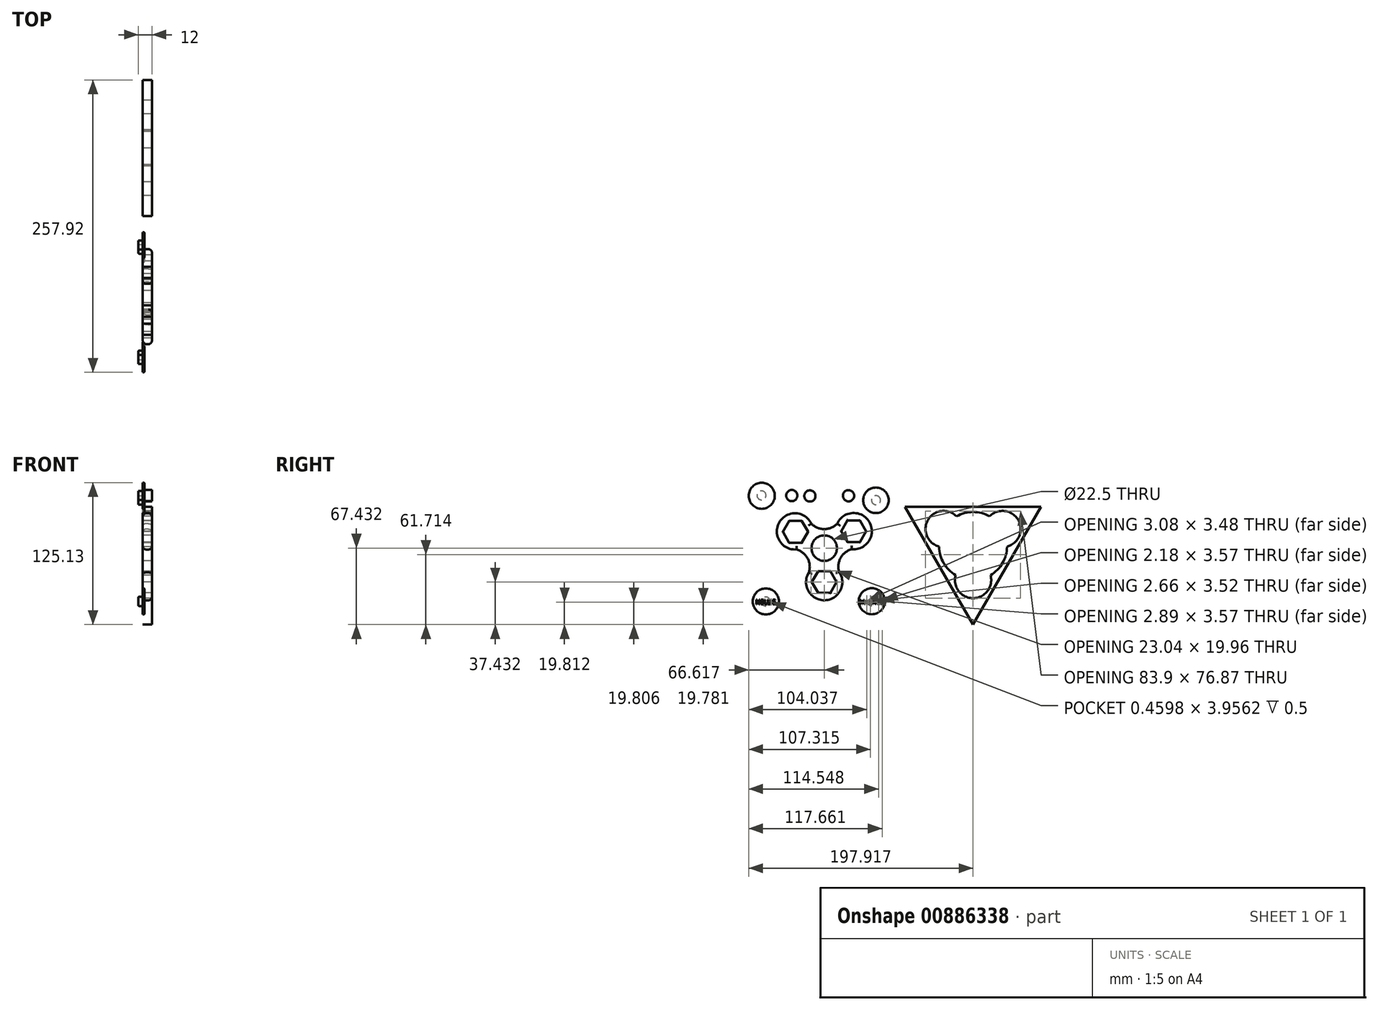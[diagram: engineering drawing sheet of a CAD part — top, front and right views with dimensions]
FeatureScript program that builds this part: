
annotation { "Feature Type Name" : "Feature", "Feature Type Description" : "" }
export const myFeature = defineFeature(function(context is Context, id is Id, definition is map)
    precondition{}
    {
        {
            var Q0;
            Q0=qCreatedBy(makeId("Right.planeOp"),FACE);
            var sketch = newSketch(context, id + "F0", { "sketchPlane" : qUnion([Q0])});
            skPoint(sketch, "E0.end.orphan", {"position": v(-35.82, -2.21) * mm});
            skPoint(sketch, "E1.0.midPoint", {"position": v(26.53, 28.89) * mm});
            skLineSegment(sketch, "E2.0", {"start": v(-31.38, 29.38) * mm, "end": v(-31.17, 29.38) * mm});
            skPoint(sketch, "E2.0.midPoint", {"position": v(-25.1, 29.46) * mm});
            skPoint(sketch, "E3.0.midPoint", {"position": v(-0.22, -15.81) * mm});
            skArc(sketch, "E4", {"start": v(24.19, 4.5) * mm, "mid": v(39.61, 28.42) * mm, "end": v(11.18, 27.02) * mm});
            skArc(sketch, "E5", {"start": v(-13.75, -16.02) * mm, "mid": v(0.24, -40.57) * mm, "end": v(12.78, -15.26) * mm});
            skPoint(sketch, "E6.startSnap0", {"position": v(-7.81, -20.2) * mm});
            skLineSegment(sketch, "E7", {"start": v(71.08, 41.9) * mm, "end": v(191.08, 41.9) * mm});
            skLineSegment(sketch, "E8", {"start": v(191.08, 41.9) * mm, "end": v(131.08, -62.01) * mm});
            skLineSegment(sketch, "E9", {"start": v(131.08, -62.01) * mm, "end": v(71.08, 41.9) * mm});
            skPoint(sketch, "E10.end.orphan", {"position": v(95.48, -0.36) * mm});
            skLineSegment(sketch, "E11", {"start": v(131.08, -62.01) * mm, "end": v(101.08, -10.05) * mm});
            skLineSegment(sketch, "E12", {"start": v(191.08, 41.9) * mm, "end": v(101.08, -10.05) * mm});
            skLineSegment(sketch, "E13", {"start": v(131.08, -62.01) * mm, "end": v(161.08, -10.05) * mm});
            skLineSegment(sketch, "E14", {"start": v(161.08, -10.05) * mm, "end": v(71.08, 41.9) * mm});
            skLineSegment(sketch, "E15", {"start": v(71.08, 41.9) * mm, "end": v(98.79, 25.9) * mm});
            skLineSegment(sketch, "E16", {"start": v(191.08, 41.9) * mm, "end": v(163.36, 25.9) * mm});
            skLineSegment(sketch, "E17", {"start": v(131.08, -62.01) * mm, "end": v(131.08, -30.01) * mm});
            skCircle(sketch, "E18", {"center": v(131.08, 7.27) * mm, "radius": 11 * mm});
            skCircle(sketch, "E19", {"center": v(131.08, 7.27) * mm, "radius": 16 * mm});
            skCircle(sketch, "E20", {"center": v(131.08, 7.27) * mm, "radius": 30 * mm});
            skCircle(sketch, "E21", {"center": v(157.06, 22.27) * mm, "radius": 11 * mm});
            skCircle(sketch, "E22", {"center": v(105.1, 22.27) * mm, "radius": 11 * mm});
            skLineSegment(sketch, "E23", {"start": v(131.08, -30.01) * mm, "end": v(131.08, 40.66) * mm});
            skCircle(sketch, "E24", {"center": v(131.08, -22.73) * mm, "radius": 11 * mm});
            skCircle(sketch, "E25.cCircle", {"center": v(157.06, 22.27) * mm, "radius": 8.96 * mm, "construction": true});
            skLineSegment(sketch, "E25.0", {"start": v(151.89, 31.23) * mm, "end": v(162.23, 31.23) * mm});
            skLineSegment(sketch, "E25.1", {"start": v(162.23, 31.23) * mm, "end": v(167.4, 22.27) * mm});
            skLineSegment(sketch, "E25.2", {"start": v(167.4, 22.27) * mm, "end": v(162.23, 13.31) * mm});
            skLineSegment(sketch, "E25.3", {"start": v(162.23, 13.31) * mm, "end": v(151.89, 13.31) * mm});
            skLineSegment(sketch, "E25.4", {"start": v(151.89, 13.31) * mm, "end": v(146.71, 22.27) * mm});
            skLineSegment(sketch, "E25.5", {"start": v(146.71, 22.27) * mm, "end": v(151.89, 31.23) * mm});
            skPoint(sketch, "E25.0.midPoint", {"position": v(157.06, 31.23) * mm});
            skCircle(sketch, "E26.cCircle", {"center": v(105.1, 22.27) * mm, "radius": 8.96 * mm, "construction": true});
            skLineSegment(sketch, "E26.0", {"start": v(99.92, 31.23) * mm, "end": v(110.27, 31.23) * mm});
            skLineSegment(sketch, "E26.1", {"start": v(110.27, 31.23) * mm, "end": v(115.44, 22.27) * mm});
            skLineSegment(sketch, "E26.2", {"start": v(115.44, 22.27) * mm, "end": v(110.27, 13.31) * mm});
            skLineSegment(sketch, "E26.3", {"start": v(110.27, 13.31) * mm, "end": v(99.92, 13.31) * mm});
            skLineSegment(sketch, "E26.4", {"start": v(99.92, 13.31) * mm, "end": v(94.75, 22.27) * mm});
            skLineSegment(sketch, "E26.5", {"start": v(94.75, 22.27) * mm, "end": v(99.92, 31.23) * mm});
            skPoint(sketch, "E26.0.midPoint", {"position": v(105.1, 31.23) * mm});
            skCircle(sketch, "E27.cCircle", {"center": v(131.08, -22.73) * mm, "radius": 8.77 * mm, "construction": true});
            skLineSegment(sketch, "E27.0", {"start": v(126.02, -13.97) * mm, "end": v(136.14, -13.97) * mm});
            skLineSegment(sketch, "E27.1", {"start": v(136.14, -13.97) * mm, "end": v(141.2, -22.73) * mm});
            skLineSegment(sketch, "E27.2", {"start": v(141.2, -22.73) * mm, "end": v(136.14, -31.5) * mm});
            skLineSegment(sketch, "E27.3", {"start": v(136.14, -31.5) * mm, "end": v(126.02, -31.5) * mm});
            skLineSegment(sketch, "E27.4", {"start": v(126.02, -31.5) * mm, "end": v(120.95, -22.73) * mm});
            skLineSegment(sketch, "E27.5", {"start": v(120.95, -22.73) * mm, "end": v(126.02, -13.97) * mm});
            skPoint(sketch, "E27.0.midPoint", {"position": v(131.08, -13.97) * mm});
            skCircle(sketch, "E28", {"center": v(157.06, 22.27) * mm, "radius": 16 * mm});
            skCircle(sketch, "E29", {"center": v(131.08, -22.73) * mm, "radius": 16 * mm});
            skCircle(sketch, "E30", {"center": v(105.1, 22.27) * mm, "radius": 16 * mm});
            skCircle(sketch, "E31", {"center": v(131.08, 7.27) * mm, "radius": 20 * mm});
            skArc(sketch, "E32", {"start": v(116.5, 33.49) * mm, "mid": v(131.08, 27.63) * mm, "end": v(145.65, 33.49) * mm});
            skArc(sketch, "E33", {"start": v(161.07, 6.78) * mm, "mid": v(148.55, -2.82) * mm, "end": v(146.5, -18.46) * mm});
            skArc(sketch, "E34", {"start": v(115.46, -18.35) * mm, "mid": v(113.52, -2.78) * mm, "end": v(101.08, 6.78) * mm});
            skPoint(sketch, "E34.startSnap0", {"position": v(123.49, -18.35) * mm});
            skArc(sketch, "E35", {"start": v(24.19, 4.5) * mm, "mid": v(14.34, -2.99) * mm, "end": v(12.78, -15.26) * mm});
            skArc(sketch, "E36", {"start": v(-11.63, 27.02) * mm, "mid": v(-0.22, 22.24) * mm, "end": v(11.18, 27.02) * mm});
            skArc(sketch, "E37.trimOffspring", {"start": v(-15.84, -20.2) * mm, "mid": v(-15.74, -20.25) * mm, "end": v(-15.64, -20.31) * mm});
            skArc(sketch, "E38.trimOffspring", {"start": v(-11.63, 27.02) * mm, "mid": v(-39.88, 28.17) * mm, "end": v(-24.78, 4.26) * mm});
            skArc(sketch, "E39.trimOffspring", {"start": v(-13.75, -16.02) * mm, "mid": v(-14.94, -3.53) * mm, "end": v(-24.78, 4.26) * mm});
            skPoint(sketch, "E2.cCircle.center.orphan", {"position": v(-25.1, 20.5) * mm});
            skPoint(sketch, "E40.orphan", {"position": v(59.78, 40.06) * mm});
            skPoint(sketch, "E41.start.orphan", {"position": v(29.78, -11.9) * mm});
            skPoint(sketch, "E42.end.orphan", {"position": v(-30.22, -11.9) * mm});
            skPoint(sketch, "E43.orphan", {"position": v(-0.22, -63.86) * mm});
            skPoint(sketch, "E44.orphan", {"position": v(-60.22, 40.06) * mm});
            skCircle(sketch, "E45", {"center": v(-0.22, 5.42) * mm, "radius": 11.25 * mm});
            skLineSegment(sketch, "E46", {"start": v(-5.33, -15.9) * mm, "end": v(-5.8, -15.1) * mm});
            skLineSegment(sketch, "E47.0", {"start": v(-5.7, -15.1) * mm, "end": v(5.25, -15.1) * mm});
            skLineSegment(sketch, "E47.1", {"start": v(5.25, -15.1) * mm, "end": v(10.72, -24.58) * mm});
            skLineSegment(sketch, "E47.2", {"start": v(10.72, -24.58) * mm, "end": v(5.25, -34.06) * mm});
            skLineSegment(sketch, "E47.3", {"start": v(5.25, -34.06) * mm, "end": v(-5.7, -34.06) * mm});
            skLineSegment(sketch, "E47.4", {"start": v(-5.7, -34.06) * mm, "end": v(-11.17, -24.58) * mm});
            skLineSegment(sketch, "E47.5", {"start": v(-11.17, -24.58) * mm, "end": v(-5.7, -15.1) * mm});
            skPoint(sketch, "E47.0.midPoint", {"position": v(-0.22, -15.1) * mm});
            skPoint(sketch, "E48.endSnap0", {"position": v(-33.8, 24.63) * mm});
            skPoint(sketch, "E2.1.start.orphan", {"position": v(-18.83, 29.53) * mm});
            skPoint(sketch, "E49.orphan", {"position": v(-36.22, 19.88) * mm});
            skPoint(sketch, "E48.end.orphan", {"position": v(-33.8, 34.15) * mm});
            skPoint(sketch, "E50.orphan", {"position": v(21.03, 28.32) * mm});
            skPoint(sketch, "E1.1.start.orphan", {"position": v(32.03, 29.46) * mm});
            skLineSegment(sketch, "E51.0", {"start": v(-31.12, 29.46) * mm, "end": v(-20, 29.46) * mm});
            skLineSegment(sketch, "E51.1", {"start": v(-20, 29.46) * mm, "end": v(-14.45, 19.84) * mm});
            skLineSegment(sketch, "E51.2", {"start": v(-14.45, 19.84) * mm, "end": v(-20, 10.21) * mm});
            skLineSegment(sketch, "E51.3", {"start": v(-20, 10.21) * mm, "end": v(-31.12, 10.21) * mm});
            skLineSegment(sketch, "E51.4", {"start": v(-31.12, 10.21) * mm, "end": v(-36.67, 19.84) * mm});
            skLineSegment(sketch, "E51.5", {"start": v(-36.67, 19.84) * mm, "end": v(-31.12, 29.46) * mm});
            skPoint(sketch, "E51.0.midPoint", {"position": v(-25.56, 29.46) * mm});
            skPoint(sketch, "E52.0.midPoint", {"position": v(25.76, 30.74) * mm});
            skLineSegment(sketch, "E53", {"start": v(-31.2, 29.32) * mm, "end": v(-31.45, 29.77) * mm});
            skLineSegment(sketch, "E54", {"start": v(36.75, 20.42) * mm, "end": v(36.76, 20.42) * mm});
            skLineSegment(sketch, "E55.0", {"start": v(20.26, 29.94) * mm, "end": v(31.25, 29.94) * mm});
            skLineSegment(sketch, "E55.1", {"start": v(31.25, 29.94) * mm, "end": v(36.75, 20.42) * mm});
            skLineSegment(sketch, "E55.2", {"start": v(36.75, 20.42) * mm, "end": v(31.25, 10.9) * mm});
            skLineSegment(sketch, "E55.3", {"start": v(31.25, 10.9) * mm, "end": v(20.26, 10.9) * mm});
            skLineSegment(sketch, "E55.4", {"start": v(20.26, 10.9) * mm, "end": v(14.77, 20.42) * mm});
            skLineSegment(sketch, "E55.5", {"start": v(14.77, 20.42) * mm, "end": v(20.26, 29.94) * mm});
            skPoint(sketch, "E55.0.midPoint", {"position": v(25.76, 29.94) * mm});
            skPoint(sketch, "E56.orphan", {"position": v(19.8, 10.1) * mm});
            skPoint(sketch, "E57.orphan", {"position": v(13.85, 20.42) * mm});
            skPoint(sketch, "E58.orphan", {"position": v(37.67, 20.42) * mm});
            skPoint(sketch, "E59.orphan", {"position": v(31.71, 30.74) * mm});
            skPoint(sketch, "E52.0.start.orphan", {"position": v(19.8, 30.74) * mm});
            skPoint(sketch, "E51.cCircle.center.orphan", {"position": v(-25.56, 19.84) * mm});
            skPoint(sketch, "E60.orphan", {"position": v(4.84, -15.81) * mm});
            skLineSegment(sketch, "E61.trimOffspring", {"start": v(-5.33, -15.9) * mm, "end": v(-5.28, -15.81) * mm});
            skPoint(sketch, "E62.orphan", {"position": v(-10.35, -24.58) * mm});
            skLineSegment(sketch, "E63.trimOffspring", {"start": v(-0.22, -15.81) * mm, "end": v(-0.22, -15.1) * mm});
            skLineSegment(sketch, "E64.trimOffspring", {"start": v(-0.22, 22.24) * mm, "end": v(-0.22, 38.8) * mm});
            skSolve(sketch);
        }
        {
            var Q0;
            Q0 = qSketchRegion(id + "F0", true);
            extrude(context, id + "F1", {"entities" : qUnion([Q0]), "depth" : 8 * mm, "offsetDistance" : 25 * mm});
        }
        {
            var Q0;
            Q0=qCreatedBy(makeId("Right.planeOp"),FACE);
            var sketch = newSketch(context, id + "F2", { "sketchPlane" : qUnion([Q0])});
            skCircle(sketch, "E65", {"center": v(-51.74, -41.64) * mm, "radius": 11.5 * mm});
            skCircle(sketch, "E66", {"center": v(-55.34, 51.62) * mm, "radius": 11.5 * mm});
            skSolve(sketch);
        }
        {
            var Q0;
            Q0 = qSketchRegion(id + "F2", true);
            extrude(context, id + "F3", {"entities" : qUnion([Q0]), "depth" : 1.5 * mm, "offsetDistance" : 25 * mm});
        }
        {
            var Q0;
            Q0=makeQuery(id+"F3.opExtrude","CAP_FACE",FACE,{"disambiguationData":[OSD([sQuery(id+"F2.wireOp",EDGE,"E65")])],"isStart":false});
            var sketch = newSketch(context, id + "F4", { "sketchPlane" : qUnion([Q0])});
            skText(sketch, "E67", { "text": "NELLIE\n", "fontName": "OpenSans-Regular.ttf"});
            const initialGuessF4  = {"E67": [-0.06069, -0.04405, 1, 0, 0.00399]};
            skSetInitialGuess(sketch, initialGuessF4);
            skSolve(sketch);
        }
        {
            var Q0;
            Q0 = qSketchRegion(id + "F4", true);
            extrude(context, id + "F5", {"entities" : qUnion([Q0]), "operationType" : NewBodyOperationType.REMOVE, "oppositeDirection" : true, "depth" : 0.5 * mm, "offsetDistance" : 25 * mm});
        }
        {
            var Q0;
            Q0=qCreatedBy(makeId("Right.planeOp"),FACE);
            var sketch = newSketch(context, id + "F6", { "sketchPlane" : qUnion([Q0])});
            skCircle(sketch, "E68", {"center": v(41.73, -41.46) * mm, "radius": 11.5 * mm});
            skCircle(sketch, "E69", {"center": v(45.36, 47.63) * mm, "radius": 11.26 * mm});
            skSolve(sketch);
        }
        {
            var Q0;
            Q0 = qSketchRegion(id + "F6", true);
            extrude(context, id + "F7", {"entities" : qUnion([Q0]), "depth" : 1.5 * mm, "offsetDistance" : 25 * mm});
        }
        {
            var Q0;
            Q0=makeQuery(id+"F7.opExtrude","CAP_FACE",FACE,{"disambiguationData":[OSD([sQuery(id+"F6.wireOp",EDGE,"E68")])],"isStart":false});
            var sketch = newSketch(context, id + "F8", { "sketchPlane" : qUnion([Q0])});
            skText(sketch, "E70", { "text": "MAGNUS", "fontName": "OpenSans-Regular.ttf"});
            const initialGuessF8  = {"E70": [0.03127, -0.04394, 1, 0, 0.0035]};
            skSetInitialGuess(sketch, initialGuessF8);
            skSolve(sketch);
        }
        {
            var Q0;
            Q0 = qSketchRegion(id + "F8", true);
            extrude(context, id + "F9", {"entities" : qUnion([Q0]), "operationType" : NewBodyOperationType.REMOVE, "oppositeDirection" : true, "depth" : 0.5 * mm, "offsetDistance" : 25 * mm});
        }
        {
            var Q0;
            Q0=makeQuery(id+"F7.opExtrude","CAP_FACE",FACE,{"disambiguationData":[OSD([sQuery(id+"F6.wireOp",EDGE,"E68")])],"isStart":true});
            var sketch = newSketch(context, id + "F10", { "sketchPlane" : qUnion([Q0])});
            skCircle(sketch, "E71", {"center": v(-41.73, -41.46) * mm, "radius": 4 * mm});
            skSolve(sketch);
        }
        {
            var Q0;
            Q0 = qSketchRegion(id + "F10", true);
            extrude(context, id + "F11", {"entities" : qUnion([Q0]), "operationType" : NewBodyOperationType.ADD, "depth" : 4 * mm, "offsetDistance" : 25 * mm});
        }
        {
            var Q0;
            Q0=makeQuery(id+"F3.opExtrude","CAP_FACE",FACE,{"disambiguationData":[OSD([sQuery(id+"F2.wireOp",EDGE,"E65")])],"isStart":true});
            var sketch = newSketch(context, id + "F12", { "sketchPlane" : qUnion([Q0])});
            skCircle(sketch, "E72", {"center": v(51.74, -41.64) * mm, "radius": 4 * mm});
            skCircle(sketch, "E73", {"center": v(-45.46, 47.7) * mm, "radius": 4 * mm});
            skCircle(sketch, "E74", {"center": v(55.55, 51.99) * mm, "radius": 4 * mm});
            skSolve(sketch);
        }
        {
            var Q0;
            Q0 = qSketchRegion(id + "F12", true);
            extrude(context, id + "F13", {"entities" : qUnion([Q0]), "operationType" : NewBodyOperationType.ADD, "depth" : 4 * mm, "offsetDistance" : 25 * mm});
        }
        {
            var Q0;
            Q0=makeQuery(id+"F1.opExtrude","CAP_EDGE",EDGE,{"disambiguationData":[OSD([sQuery(id+"F0.wireOp",EDGE,"E4")])],"isStart":false});
            var Q1;
            Q1=makeQuery(id+"F1.opExtrude","CAP_EDGE",EDGE,{"disambiguationData":[OSD([sQuery(id+"F0.wireOp",EDGE,"E36")])],"isStart":false});
            var Q2;
            Q2=makeQuery(id+"F1.opExtrude","CAP_EDGE",EDGE,{"disambiguationData":[OSD([sQuery(id+"F0.wireOp",EDGE,"E39.trimOffspring")])],"isStart":false});
            var Q3;
            Q3=makeQuery(id+"F1.opExtrude","CAP_EDGE",EDGE,{"disambiguationData":[OSD([sQuery(id+"F0.wireOp",EDGE,"E35")])],"isStart":false});
            var Q4;
            Q4=makeQuery(id+"F1.opExtrude","CAP_EDGE",EDGE,{"disambiguationData":[OSD([sQuery(id+"F0.wireOp",EDGE,"E5")])],"isStart":false});
            var Q5;
            Q5=makeQuery(id+"F1.opExtrude","CAP_EDGE",EDGE,{"disambiguationData":[OSD([sQuery(id+"F0.wireOp",EDGE,"E38.trimOffspring")])],"isStart":false});
            var Q6;
            Q6=makeQuery(id+"F1.opExtrude","CAP_EDGE",EDGE,{"disambiguationData":[OSD([sQuery(id+"F0.wireOp",EDGE,"E36")])],"isStart":true});
            var Q7;
            Q7=makeQuery(id+"F1.opExtrude","CAP_EDGE",EDGE,{"disambiguationData":[OSD([sQuery(id+"F0.wireOp",EDGE,"E4")])],"isStart":true});
            var Q8;
            Q8=makeQuery(id+"F1.opExtrude","CAP_EDGE",EDGE,{"disambiguationData":[OSD([sQuery(id+"F0.wireOp",EDGE,"E35")])],"isStart":true});
            var Q9;
            Q9=makeQuery(id+"F1.opExtrude","CAP_EDGE",EDGE,{"disambiguationData":[OSD([sQuery(id+"F0.wireOp",EDGE,"E39.trimOffspring")])],"isStart":true});
            var Q10;
            Q10=makeQuery(id+"F1.opExtrude","CAP_EDGE",EDGE,{"disambiguationData":[OSD([sQuery(id+"F0.wireOp",EDGE,"E38.trimOffspring")])],"isStart":true});
            var Q11;
            Q11=makeQuery(id+"F1.opExtrude","CAP_EDGE",EDGE,{"disambiguationData":[OSD([sQuery(id+"F0.wireOp",EDGE,"E5")])],"isStart":true});
            fillet(context, id + "F14", {"entities" : qUnion([Q0, Q1, Q2, Q3, Q4, Q5, Q6, Q7, Q8, Q9, Q10, Q11]), "radius" : 3 * mm, "tangentPropagation" : true, "allowEdgeOverflow" : false});
        }
        {
            var Q0;
            Q0=makeQuery(id+"F3.opExtrude","CAP_EDGE",EDGE,{"disambiguationData":[OSD([sQuery(id+"F2.wireOp",EDGE,"E65")])],"isStart":false});
            var Q1;
            Q1=makeQuery(id+"F7.opExtrude","CAP_EDGE",EDGE,{"disambiguationData":[OSD([sQuery(id+"F6.wireOp",EDGE,"E68")])],"isStart":false});
            var Q2;
            Q2=makeQuery(id+"F13.opExtrude","CAP_EDGE",EDGE,{"disambiguationData":[OSD([sQuery(id+"F12.wireOp",EDGE,"E72")])],"isStart":false});
            var Q3;
            Q3=makeQuery(id+"F11.opExtrude","CAP_EDGE",EDGE,{"disambiguationData":[OSD([sQuery(id+"F10.wireOp",EDGE,"E71")])],"isStart":false});
            var Q4;
            Q4=makeQuery(id+"F3.opExtrude","CAP_EDGE",EDGE,{"disambiguationData":[OSD([sQuery(id+"F2.wireOp",EDGE,"E66")])],"isStart":false});
            var Q5;
            Q5=makeQuery(id+"F7.opExtrude","CAP_EDGE",EDGE,{"disambiguationData":[OSD([sQuery(id+"F6.wireOp",EDGE,"E69")])],"isStart":false});
            fillet(context, id + "F15", {"entities" : qUnion([Q0, Q1, Q2, Q3, Q4, Q5]), "radius" : 0.8 * mm, "tangentPropagation" : true, "allowEdgeOverflow" : false});
        }
        {
            var Q0;
            Q0=makeQuery(id+"F1.opExtrude","CAP_EDGE",EDGE,{"disambiguationData":[OSD([sQuery(id+"F0.wireOp",EDGE,"E51.4")])],"isStart":false});
            var Q1;
            Q1=makeQuery(id+"F1.opExtrude","CAP_EDGE",EDGE,{"disambiguationData":[OSD([sQuery(id+"F0.wireOp",EDGE,"E51.0")])],"isStart":false});
            var Q2;
            Q2=makeQuery(id+"F1.opExtrude","CAP_EDGE",EDGE,{"disambiguationData":[OSD([sQuery(id+"F0.wireOp",EDGE,"E51.1")])],"isStart":false});
            var Q3;
            Q3=makeQuery(id+"F1.opExtrude","CAP_EDGE",EDGE,{"disambiguationData":[OSD([sQuery(id+"F0.wireOp",EDGE,"E51.2")])],"isStart":false});
            var Q4;
            Q4=makeQuery(id+"F1.opExtrude","CAP_EDGE",EDGE,{"disambiguationData":[OSD([sQuery(id+"F0.wireOp",EDGE,"E55.5")])],"isStart":false});
            var Q5;
            Q5=makeQuery(id+"F1.opExtrude","CAP_EDGE",EDGE,{"disambiguationData":[OSD([sQuery(id+"F0.wireOp",EDGE,"E55.3")])],"isStart":false});
            var Q6;
            Q6=makeQuery(id+"F1.opExtrude","CAP_EDGE",EDGE,{"disambiguationData":[OSD([sQuery(id+"F0.wireOp",EDGE,"E55.2")])],"isStart":false});
            var Q7;
            Q7=makeQuery(id+"F1.opExtrude","CAP_EDGE",EDGE,{"disambiguationData":[OSD([sQuery(id+"F0.wireOp",EDGE,"E55.1")])],"isStart":false});
            var Q8;
            Q8=makeQuery(id+"F1.opExtrude","CAP_EDGE",EDGE,{"disambiguationData":[OSD([sQuery(id+"F0.wireOp",EDGE,"E55.0")])],"isStart":false});
            var Q9;
            Q9=makeQuery(id+"F1.opExtrude","CAP_EDGE",EDGE,{"disambiguationData":[OSD([sQuery(id+"F0.wireOp",EDGE,"E47.0")])],"isStart":false});
            var Q10;
            Q10=makeQuery(id+"F1.opExtrude","CAP_EDGE",EDGE,{"disambiguationData":[OSD([sQuery(id+"F0.wireOp",EDGE,"E47.5")])],"isStart":false});
            var Q11;
            Q11=makeQuery(id+"F1.opExtrude","CAP_EDGE",EDGE,{"disambiguationData":[OSD([sQuery(id+"F0.wireOp",EDGE,"E47.4")])],"isStart":false});
            var Q12;
            Q12=makeQuery(id+"F1.opExtrude","CAP_EDGE",EDGE,{"disambiguationData":[OSD([sQuery(id+"F0.wireOp",EDGE,"E47.3")])],"isStart":false});
            var Q13;
            Q13=makeQuery(id+"F1.opExtrude","CAP_EDGE",EDGE,{"disambiguationData":[OSD([sQuery(id+"F0.wireOp",EDGE,"E47.2")])],"isStart":false});
            var Q14;
            Q14=makeQuery(id+"F1.opExtrude","CAP_EDGE",EDGE,{"disambiguationData":[OSD([sQuery(id+"F0.wireOp",EDGE,"E47.1")])],"isStart":false});
            var Q15;
            Q15=makeQuery(id+"F1.opExtrude","CAP_EDGE",EDGE,{"disambiguationData":[OSD([sQuery(id+"F0.wireOp",EDGE,"E55.2")])],"isStart":true});
            var Q16;
            Q16=makeQuery(id+"F1.opExtrude","CAP_EDGE",EDGE,{"disambiguationData":[OSD([sQuery(id+"F0.wireOp",EDGE,"E55.0")])],"isStart":true});
            var Q17;
            Q17=makeQuery(id+"F1.opExtrude","CAP_EDGE",EDGE,{"disambiguationData":[OSD([sQuery(id+"F0.wireOp",EDGE,"E55.5")])],"isStart":true});
            var Q18;
            Q18=makeQuery(id+"F1.opExtrude","CAP_EDGE",EDGE,{"disambiguationData":[OSD([sQuery(id+"F0.wireOp",EDGE,"E55.3")])],"isStart":true});
            var Q19;
            Q19=makeQuery(id+"F1.opExtrude","CAP_EDGE",EDGE,{"disambiguationData":[OSD([sQuery(id+"F0.wireOp",EDGE,"E51.2")])],"isStart":true});
            var Q20;
            Q20=makeQuery(id+"F1.opExtrude","CAP_EDGE",EDGE,{"disambiguationData":[OSD([sQuery(id+"F0.wireOp",EDGE,"E51.0")])],"isStart":true});
            var Q21;
            Q21=makeQuery(id+"F1.opExtrude","CAP_EDGE",EDGE,{"disambiguationData":[OSD([sQuery(id+"F0.wireOp",EDGE,"E51.4")])],"isStart":true});
            var Q22;
            Q22=makeQuery(id+"F1.opExtrude","CAP_EDGE",EDGE,{"disambiguationData":[OSD([sQuery(id+"F0.wireOp",EDGE,"E51.3")])],"isStart":true});
            var Q23;
            Q23=makeQuery(id+"F1.opExtrude","CAP_EDGE",EDGE,{"disambiguationData":[OSD([sQuery(id+"F0.wireOp",EDGE,"E47.0")])],"isStart":true});
            var Q24;
            Q24=makeQuery(id+"F1.opExtrude","CAP_EDGE",EDGE,{"disambiguationData":[OSD([sQuery(id+"F0.wireOp",EDGE,"E47.5")])],"isStart":true});
            var Q25;
            Q25=makeQuery(id+"F1.opExtrude","CAP_EDGE",EDGE,{"disambiguationData":[OSD([sQuery(id+"F0.wireOp",EDGE,"E47.4")])],"isStart":true});
            var Q26;
            Q26=makeQuery(id+"F1.opExtrude","CAP_EDGE",EDGE,{"disambiguationData":[OSD([sQuery(id+"F0.wireOp",EDGE,"E47.3")])],"isStart":true});
            var Q27;
            Q27=makeQuery(id+"F1.opExtrude","CAP_EDGE",EDGE,{"disambiguationData":[OSD([sQuery(id+"F0.wireOp",EDGE,"E47.2")])],"isStart":true});
            var Q28;
            Q28=makeQuery(id+"F1.opExtrude","CAP_EDGE",EDGE,{"disambiguationData":[OSD([sQuery(id+"F0.wireOp",EDGE,"E47.1")])],"isStart":true});
            var Q29;
            Q29=makeQuery(id+"F1.opExtrude","CAP_EDGE",EDGE,{"disambiguationData":[OSD([sQuery(id+"F0.wireOp",EDGE,"E51.5")])],"isStart":true});
            var Q30;
            Q30=makeQuery(id+"F1.opExtrude","CAP_EDGE",EDGE,{"disambiguationData":[OSD([sQuery(id+"F0.wireOp",EDGE,"E55.4")])],"isStart":true});
            var Q31;
            Q31=makeQuery(id+"F1.opExtrude","CAP_EDGE",EDGE,{"disambiguationData":[OSD([sQuery(id+"F0.wireOp",EDGE,"E51.1")])],"isStart":true});
            var Q32;
            Q32=makeQuery(id+"F1.opExtrude","CAP_EDGE",EDGE,{"disambiguationData":[OSD([sQuery(id+"F0.wireOp",EDGE,"E55.1")])],"isStart":true});
            fillet(context, id + "F16", {"entities" : qUnion([Q0, Q1, Q2, Q3, Q4, Q5, Q6, Q7, Q8, Q9, Q10, Q11, Q12, Q13, Q14, Q15, Q16, Q17, Q18, Q19, Q20, Q21, Q22, Q23, Q24, Q25, Q26, Q27, Q28, Q29, Q30, Q31, Q32]), "radius" : 0.5 * mm, "tangentPropagation" : true, "allowEdgeOverflow" : false});
        }
        {
            var Q0;
            Q0=qCreatedBy(makeId("Right.planeOp"),FACE);
            var sketch = newSketch(context, id + "F17", { "sketchPlane" : qUnion([Q0])});
            skCircle(sketch, "E75", {"center": v(21.23, 51.62) * mm, "radius": 4.95 * mm});
            skCircle(sketch, "E76", {"center": v(-12.88, 51.44) * mm, "radius": 4.95 * mm});
            skCircle(sketch, "E77", {"center": v(-28.86, 51.8) * mm, "radius": 4.95 * mm});
            skSolve(sketch);
        }
        {
            var Q0;
            Q0 = qSketchRegion(id + "F17", true);
            extrude(context, id + "F18", {"entities" : qUnion([Q0]), "depth" : 8 * mm, "offsetDistance" : 25 * mm});
        }
        {
            var Q0;
            Q0=makeQuery(id+"F7.opExtrude","SWEPT_BODY",BODY,{"disambiguationData":[OSD([sQuery(id+"F6.wireOp",EDGE,"E68")])]});
            transform(context, id + "F19", {"entities" : qUnion([Q0]), "transformType" : TransformType.COPY});
        }
    });
